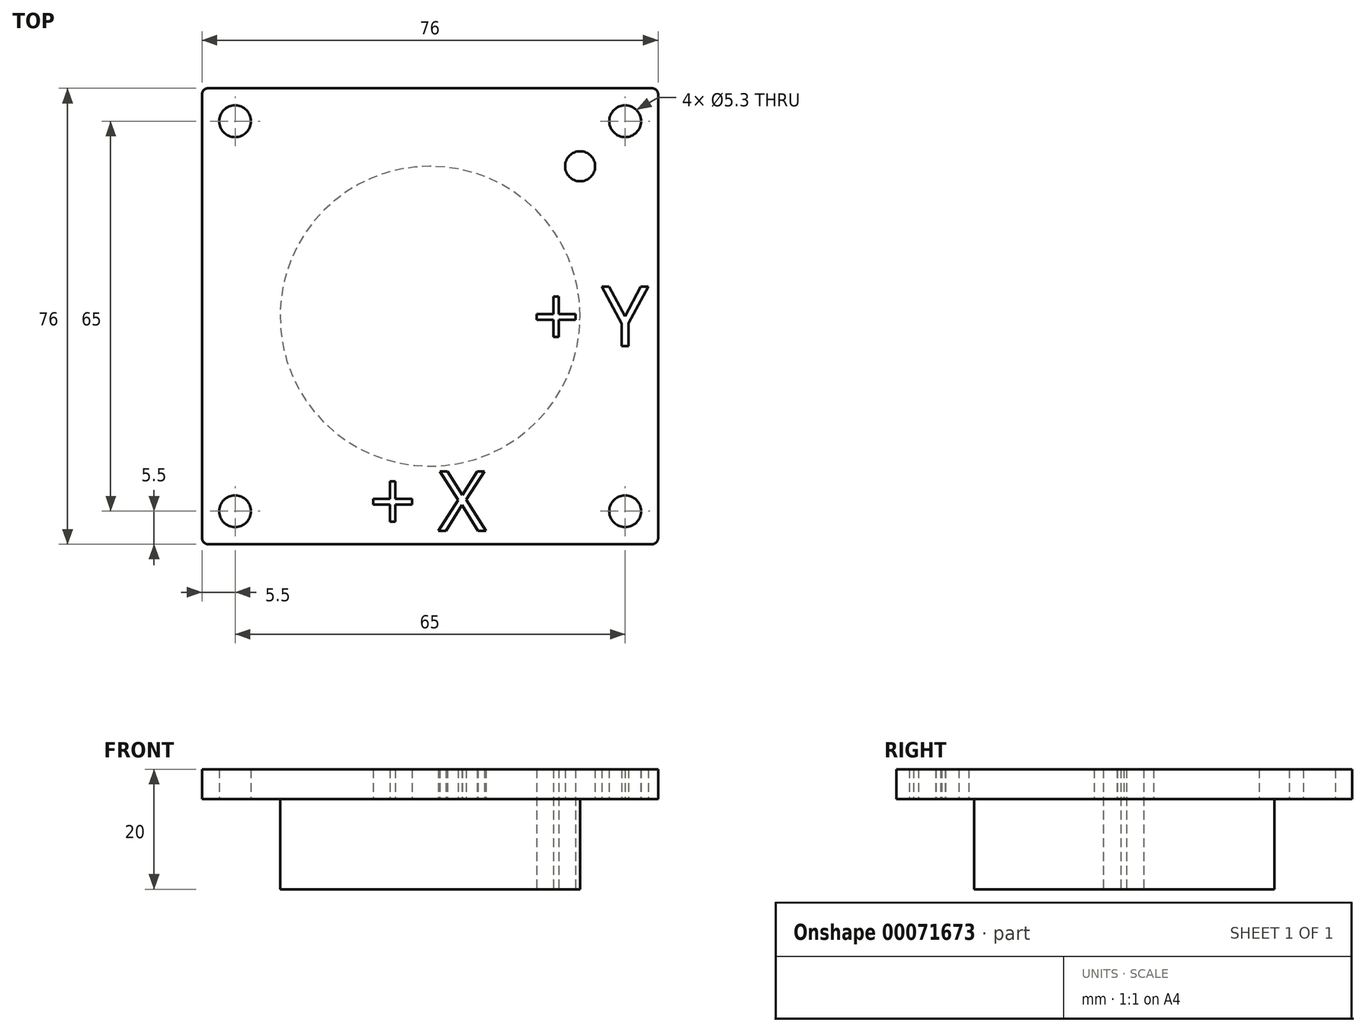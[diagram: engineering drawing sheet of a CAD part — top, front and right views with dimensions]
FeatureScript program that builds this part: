
annotation { "Feature Type Name" : "Feature", "Feature Type Description" : "" }
export const myFeature = defineFeature(function(context is Context, id is Id, definition is map)
    precondition{}
    {
        {
            var Q0;
            Q0=qCreatedBy(makeId("Top.planeOp"),FACE);
            var sketch = newSketch(context, id + "F0", { "sketchPlane" : qUnion([Q0])});
            skLineSegment(sketch, "E0.bottom", {"start": v(-37, 38) * mm, "end": v(37, 38) * mm});
            skLineSegment(sketch, "E0.top", {"start": v(-37, -38) * mm, "end": v(37, -38) * mm});
            skLineSegment(sketch, "E0.left", {"start": v(-38, 37) * mm, "end": v(-38, -37) * mm});
            skLineSegment(sketch, "E0.right", {"start": v(38, 37) * mm, "end": v(38, -37) * mm});
            skCircle(sketch, "E1", {"center": v(32.5, 32.5) * mm, "radius": 2.65 * mm});
            skCircle(sketch, "E2", {"center": v(32.5, -32.5) * mm, "radius": 2.65 * mm});
            skCircle(sketch, "E3", {"center": v(-32.5, 32.5) * mm, "radius": 2.65 * mm});
            skCircle(sketch, "E4", {"center": v(-32.5, -32.5) * mm, "radius": 2.65 * mm});
            skLineSegment(sketch, "E5", {"start": v(0, 0) * mm, "end": v(38, 38) * mm, "construction": true});
            skCircle(sketch, "E6", {"center": v(25, 25) * mm, "radius": 2.5 * mm});
            skPoint(sketch, "E7.visualSharp", {"position": v(38, 38) * mm});
            skArc(sketch, "E7.filletArc", {"start": v(38, 37) * mm, "mid": v(37.7, 37.7) * mm, "end": v(37, 38) * mm});
            skPoint(sketch, "E8.visualSharp", {"position": v(-38, 38) * mm});
            skArc(sketch, "E8.filletArc", {"start": v(-37, 38) * mm, "mid": v(-37.7, 37.7) * mm, "end": v(-38, 37) * mm});
            skPoint(sketch, "E9.visualSharp", {"position": v(38, -38) * mm});
            skArc(sketch, "E9.filletArc", {"start": v(37, -38) * mm, "mid": v(37.7, -37.7) * mm, "end": v(38, -37) * mm});
            skPoint(sketch, "E10.visualSharp", {"position": v(-38, -38) * mm});
            skArc(sketch, "E10.filletArc", {"start": v(-38, -37) * mm, "mid": v(-37.7, -37.7) * mm, "end": v(-37, -38) * mm});
            skText(sketch, "E11", { "text": "+ X", "fontName": "OpenSans-Regular.ttf"});
            skText(sketch, "E12", { "text": "+ Y", "fontName": "OpenSans-Regular.ttf"});
            skCircle(sketch, "E13", {"center": v(0, 0) * mm, "radius": 25 * mm});
            const initialGuessF0  = {"E11": [-0.0102, -0.0358, 1, 0, 0.01], "E12": [0.01704, -0.005, 1, 0, 0.01]};
            skSetInitialGuess(sketch, initialGuessF0);
            skSolve(sketch);
        }
        {
            var Q0;
            Q0=makeQuery(id+"F0.imprint","IMPRINT",FACE,{"disambiguationData":[TD([[makeQuery(id+"F0.imprint","IMPRINT",EDGE,{"derivedFrom":sQuery(id+"F0.wireOp",EDGE,"E0.bottom")}),-1.0]])]});
            var Q1;
            Q1=makeQuery(id+"F0.imprint","IMPRINT",FACE,{"disambiguationData":[TD([[makeQuery(id+"F0.imprint","IMPRINT",EDGE,{"derivedFrom":sQuery(id+"F0.wireOp",EDGE,"E12.sketch_text.stroke-0")}),1.0]])]});
            extrude(context, id + "F1", {"entities" : qUnion([Q0, Q1]), "depth" : 20 * mm, "hasSecondDirection" : true, "secondDirectionOppositeDirection" : false, "secondDirectionDepth" : 15 * mm});
        }
        {
            var Q0;
            Q0=makeQuery(id+"F0.imprint","IMPRINT",FACE,{"disambiguationData":[TD([[makeQuery(id+"F0.imprint","IMPRINT",EDGE,{"derivedFrom":sQuery(id+"F0.wireOp",EDGE,"E12.sketch_text.stroke-0")}),1.0]])]});
            extrude(context, id + "F2", {"entities" : qUnion([Q0]), "operationType" : NewBodyOperationType.ADD, "depth" : 15 * mm});
        }
    });
